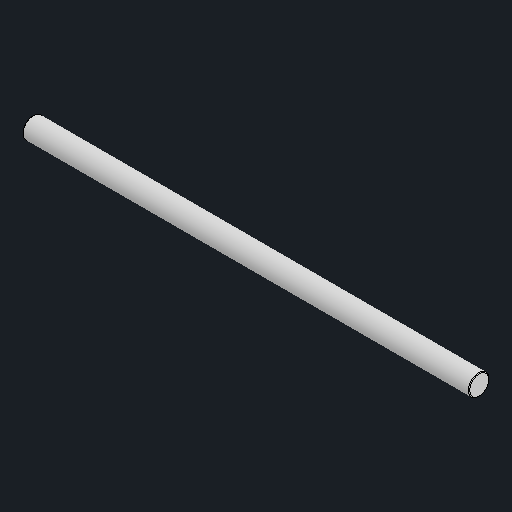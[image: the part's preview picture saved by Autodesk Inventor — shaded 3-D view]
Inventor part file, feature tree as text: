
AUTODESK INVENTOR PART (.ipt)
format: ipt  version: 2024.2 (Build 282272000, 272)  size: 74,752 bytes
history: native  units: mm
features: other x1, chamfer x1
ambient origin geometry x8: Origin, YZ Plane, XZ Plane, XY Plane, X Axis, Y Axis, Z Axis, Center Point
bodies: Body1 (feature_tree)
feature tree (2):
  other  "솔리드1"
  chamfer  "Chamfer1"  [1 undecoded]
note: 1 required parameter value undecoded (feature->parameter linkage not recoverable at this tier; creation-order binding heuristic only, values carry confidence <= 0.55)
